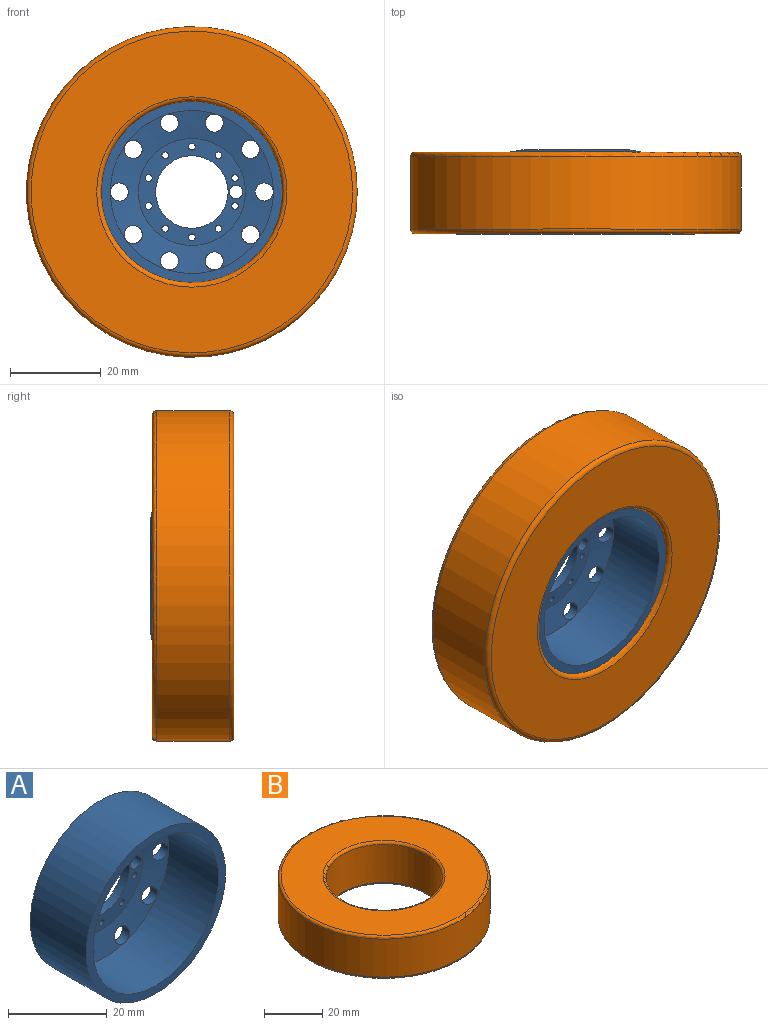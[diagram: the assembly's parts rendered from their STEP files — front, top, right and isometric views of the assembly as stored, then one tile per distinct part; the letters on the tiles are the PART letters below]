
ASSEMBLY  parts=2 mates=1
PART A: 29 faces, bbox 40x17.5x40 mm
  f0: plane 23.63x23.63mm, normal (0,-1,0), area 212.7mm2, adj f1,f10,f11,f12,f13,f14,f15,f16
  f1: cone r=14.91mm half-angle=79.4deg, axis (0,-1,0), area 464.1mm2, adj f0,f2,f4,f5,f8,f21,f22,f23
  f2: cylinder r=2mm len=4mm, axis (0,1,0), area 26.6mm2, adj f1,f3
  f3: cone r=16mm half-angle=79.4deg, axis (0,-1,0), area 691.6mm2, adj f2,f4,f5,f6,f9,f21,f22,f23
  f4: cylinder r=2mm len=4mm, axis (0,1,0), area 25.6mm2, adj f1,f3
  f5: cylinder r=2mm len=4mm, axis (0,1,0), area 25.6mm2, adj f1,f3
  f6: cylinder r=20mm len=40mm, axis (0,-1,0), area 2010.6mm2, adj f3,f7
  f7: plane 40x40mm, normal (0,-1,0), area 238.8mm2, adj f6,f8
  f8: cylinder r=18mm len=36mm, axis (0,-1,0), area 1621.8mm2, adj f1,f7
  f9: plane 24x24mm, normal (0,1,0), area 226.6mm2, adj f3,f10,f11,f12,f13,f14,f15,f16
  f10: cylinder r=8mm len=16mm, axis (0,-1,0), area 100.5mm2, adj f0,f9
  f11: cylinder r=0.75mm len=2mm, axis (0,1,0), area 9.4mm2, adj f0,f9
  f12: cylinder r=0.75mm len=2mm, axis (0,1,0), area 9.4mm2, adj f0,f9
  f13: cylinder r=0.75mm len=2mm, axis (0,1,0), area 9.4mm2, adj f0,f9
  f14: cylinder r=0.75mm len=2mm, axis (0,1,0), area 9.4mm2, adj f0,f9
  f15: cylinder r=0.75mm len=2mm, axis (0,1,0), area 9.4mm2, adj f0,f9
  f16: cylinder r=0.75mm len=2mm, axis (0,1,0), area 9.4mm2, adj f0,f9
  f17: cylinder r=0.75mm len=2mm, axis (0,1,0), area 9.4mm2, adj f0,f9
  f18: cylinder r=0.75mm len=2mm, axis (0,1,0), area 9.4mm2, adj f0,f9
  f19: cylinder r=0.75mm len=2mm, axis (0,1,0), area 9.4mm2, adj f0,f9
  f20: cylinder r=0.75mm len=2mm, axis (0,1,0), area 9.4mm2, adj f0,f9
  f21: cylinder r=2mm len=4mm, axis (0,1,0), area 26.6mm2, adj f1,f3
  f22: cylinder r=2mm len=4mm, axis (0,1,0), area 26.2mm2, adj f1,f3
  f23: cylinder r=2mm len=4mm, axis (0,1,0), area 26.2mm2, adj f1,f3
  f24: cylinder r=2mm len=4mm, axis (0,1,0), area 26.6mm2, adj f1,f3
  f25: cylinder r=2mm len=4mm, axis (0,1,0), area 26.2mm2, adj f1,f3
  f26: cylinder r=2mm len=4mm, axis (0,1,0), area 26.2mm2, adj f1,f3
  f27: cylinder r=2mm len=4mm, axis (0,1,0), area 26.6mm2, adj f1,f3
  f28: cylinder r=1.5mm len=3mm, axis (0,1,0), area 18.8mm2, adj f0,f9
PART B: 8 faces, bbox 79x79x18 mm
  f0: plane 71x71mm, normal (0,0,-1), area 2573.7mm2, adj f1,f7
  f1: torus R=21mm, axis (0,0,-1), area 201mm2, adj f0,f2
  f2: cylinder r=20mm len=40mm, axis (0,0,-1), area 2010.6mm2, adj f1,f3
  f3: torus R=21mm, axis (0,0,-1), area 201mm2, adj f2,f4
  f4: plane 71x71mm, normal (0,0,1), area 2573.7mm2, adj f3,f5
  f5: torus R=35.5mm, axis (0,0,1), area 356.7mm2, adj f4,f6
  f6: cylinder r=36.5mm len=73mm, axis (0,0,1), area 3669.4mm2, adj f5,f7
  f7: torus R=35.5mm, axis (0,0,1), area 356.7mm2, adj f0,f6
PLACE A at identity fixed
PLACE B rot(axis=(-1,0,0),90deg) t=(0,-1,0)mm
MATE fastened A.f1 <-> B.f1  axis (0,-1,0) through (0,8,0)mm
